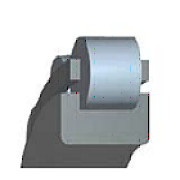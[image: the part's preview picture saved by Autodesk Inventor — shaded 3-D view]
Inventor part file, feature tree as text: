
AUTODESK INVENTOR PART (.ipt)
format: ipt  version: 2022 (Build 260153000, 153)  size: 161,792 bytes
history: native  units: mm (DEFAULTED — no unit token found)
features: other x1, sketch x1
ambient origin geometry x8: Origin, YZ Plane, XZ Plane, XY Plane, X Axis, Y Axis, Z Axis, Center Point
bodies: Solid1 (feature_tree)
feature tree (2):
  other  "轴承体"
  sketch  "草图"  dims[d0=3.0mm d1=3.0mm d2=4.333333mm d3=7.0mm d4=90.0deg d5=0.1mm d6=0.0mm d7=0.0mm d8=0.0mm d9=0.0mm d10=0.0mm]
